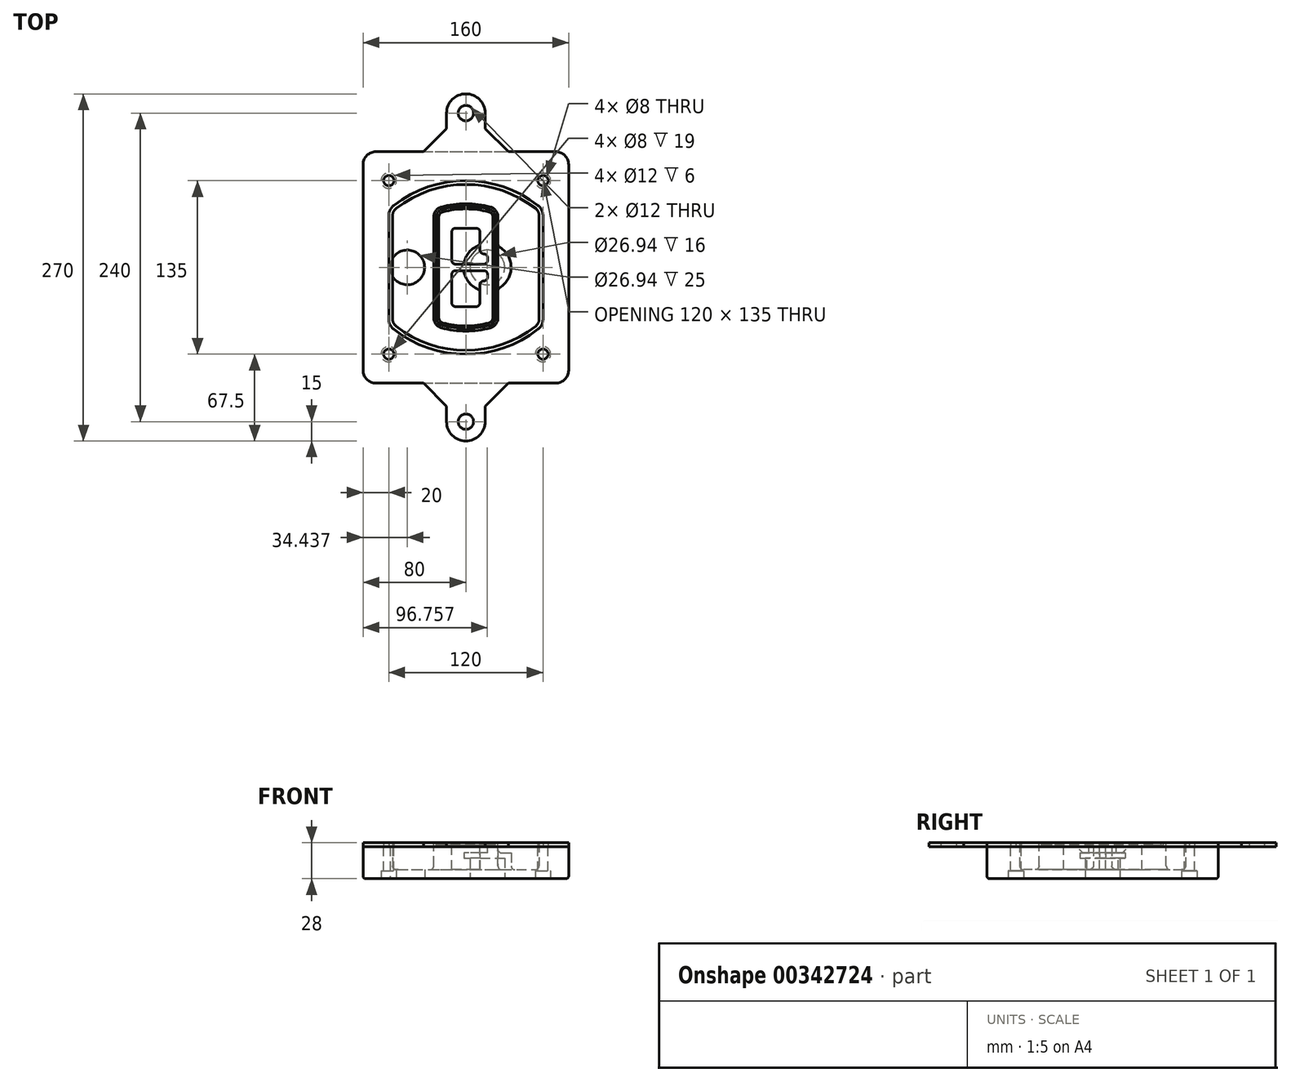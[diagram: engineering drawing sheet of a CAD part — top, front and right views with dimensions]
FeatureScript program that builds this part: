
annotation { "Feature Type Name" : "Feature", "Feature Type Description" : "" }
export const myFeature = defineFeature(function(context is Context, id is Id, definition is map)
    precondition{}
    {
        {
            var Q0;
            Q0=qCreatedBy(makeId("Top.planeOp"),FACE);
            var sketch = newSketch(context, id + "F0", { "sketchPlane" : qUnion([Q0])});
            skPoint(sketch, "E0.rect.middle", {"position": v(0, 0) * mm});
            skLineSegment(sketch, "E1.bottom", {"start": v(-70, -90) * mm, "end": v(70, -90) * mm});
            skLineSegment(sketch, "E1.top", {"start": v(-70, 90) * mm, "end": v(70, 90) * mm});
            skLineSegment(sketch, "E1.left", {"start": v(-80, -80) * mm, "end": v(-80, 80) * mm});
            skLineSegment(sketch, "E1.right", {"start": v(80, -80) * mm, "end": v(80, 80) * mm});
            skLineSegment(sketch, "E2", {"start": v(-80, 90) * mm, "end": v(80, -90) * mm, "construction": true});
            skLineSegment(sketch, "E3", {"start": v(80, 90) * mm, "end": v(-80, -90) * mm, "construction": true});
            skCircle(sketch, "E4", {"center": v(-60, 67.5) * mm, "radius": 4 * mm});
            skCircle(sketch, "E5", {"center": v(60, 67.5) * mm, "radius": 4 * mm});
            skCircle(sketch, "E6", {"center": v(60, -67.5) * mm, "radius": 4 * mm});
            skCircle(sketch, "E7", {"center": v(-60, -67.5) * mm, "radius": 4 * mm});
            skLineSegment(sketch, "E8", {"start": v(-60, 67.5) * mm, "end": v(60, 67.5) * mm, "construction": true});
            skLineSegment(sketch, "E9", {"start": v(60, 67.5) * mm, "end": v(60, -67.5) * mm, "construction": true});
            skLineSegment(sketch, "E10", {"start": v(60, -67.5) * mm, "end": v(-60, -67.5) * mm, "construction": true});
            skLineSegment(sketch, "E11", {"start": v(-60, -67.5) * mm, "end": v(-60, 67.5) * mm, "construction": true});
            skLineSegment(sketch, "E12", {"start": v(-60, 40.3) * mm, "end": v(-60, -40.3) * mm});
            skLineSegment(sketch, "E13", {"start": v(60, 40.3) * mm, "end": v(60, -40.3) * mm});
            skArc(sketch, "E14", {"start": v(56.15, 48.18) * mm, "mid": v(0, 67.5) * mm, "end": v(-56.15, 48.18) * mm});
            skArc(sketch, "E15", {"start": v(-56.15, -48.18) * mm, "mid": v(0, -67.5) * mm, "end": v(56.15, -48.18) * mm});
            skLineSegment(sketch, "E16", {"start": v(-60, 0) * mm, "end": v(60, 0) * mm, "construction": true});
            skPoint(sketch, "E17.visualSharp", {"position": v(-60, -45) * mm});
            skArc(sketch, "E17.filletArc", {"start": v(-60, -40.3) * mm, "mid": v(-58.99, -44.68) * mm, "end": v(-56.15, -48.18) * mm});
            skPoint(sketch, "E18.visualSharp", {"position": v(-60, 45) * mm});
            skArc(sketch, "E18.filletArc", {"start": v(-56.15, 48.18) * mm, "mid": v(-58.99, 44.68) * mm, "end": v(-60, 40.3) * mm});
            skPoint(sketch, "E19.visualSharp", {"position": v(60, 45) * mm});
            skArc(sketch, "E19.filletArc", {"start": v(60, 40.3) * mm, "mid": v(58.99, 44.68) * mm, "end": v(56.15, 48.18) * mm});
            skPoint(sketch, "E20.visualSharp", {"position": v(60, -45) * mm});
            skArc(sketch, "E20.filletArc", {"start": v(56.15, -48.18) * mm, "mid": v(58.99, -44.68) * mm, "end": v(60, -40.3) * mm});
            skPoint(sketch, "E21.visualSharp", {"position": v(-80, 90) * mm});
            skArc(sketch, "E21.filletArc", {"start": v(-70, 90) * mm, "mid": v(-77.07, 87.07) * mm, "end": v(-80, 80) * mm});
            skPoint(sketch, "E22.visualSharp", {"position": v(80, 90) * mm});
            skArc(sketch, "E22.filletArc", {"start": v(80, 80) * mm, "mid": v(77.07, 87.07) * mm, "end": v(70, 90) * mm});
            skPoint(sketch, "E23.visualSharp", {"position": v(80, -90) * mm});
            skArc(sketch, "E23.filletArc", {"start": v(70, -90) * mm, "mid": v(77.07, -87.07) * mm, "end": v(80, -80) * mm});
            skPoint(sketch, "E24.visualSharp", {"position": v(-80, -90) * mm});
            skArc(sketch, "E24.filletArc", {"start": v(-80, -80) * mm, "mid": v(-77.07, -87.07) * mm, "end": v(-70, -90) * mm});
            skArc(sketch, "E25.0", {"start": v(57, 40.3) * mm, "mid": v(56.3, 43.36) * mm, "end": v(54.3, 45.81) * mm});
            skLineSegment(sketch, "E25.1", {"start": v(57, 40.3) * mm, "end": v(57, -40.3) * mm});
            skArc(sketch, "E25.2", {"start": v(54.3, -45.81) * mm, "mid": v(56.3, -43.36) * mm, "end": v(57, -40.3) * mm});
            skArc(sketch, "E25.3", {"start": v(-54.3, -45.81) * mm, "mid": v(0, -64.5) * mm, "end": v(54.3, -45.81) * mm});
            skArc(sketch, "E25.4", {"start": v(-57, -40.3) * mm, "mid": v(-56.3, -43.36) * mm, "end": v(-54.3, -45.81) * mm});
            skArc(sketch, "E25.5", {"start": v(54.3, 45.81) * mm, "mid": v(0, 64.5) * mm, "end": v(-54.3, 45.81) * mm});
            skLineSegment(sketch, "E25.6", {"start": v(-57, 40.3) * mm, "end": v(-57, -40.3) * mm});
            skArc(sketch, "E25.7", {"start": v(-54.3, 45.81) * mm, "mid": v(-56.3, 43.36) * mm, "end": v(-57, 40.3) * mm});
            skArc(sketch, "E26.0", {"start": v(-58.62, 51.33) * mm, "mid": v(-62.58, 46.43) * mm, "end": v(-64, 40.3) * mm});
            skArc(sketch, "E26.1", {"start": v(58.62, 51.33) * mm, "mid": v(0, 71.5) * mm, "end": v(-58.62, 51.33) * mm});
            skArc(sketch, "E26.2", {"start": v(64, 40.3) * mm, "mid": v(62.58, 46.43) * mm, "end": v(58.62, 51.33) * mm});
            skLineSegment(sketch, "E26.3", {"start": v(64, 40.3) * mm, "end": v(64, -40.3) * mm});
            skArc(sketch, "E26.4", {"start": v(58.62, -51.33) * mm, "mid": v(62.58, -46.43) * mm, "end": v(64, -40.3) * mm});
            skLineSegment(sketch, "E26.5", {"start": v(-64, 40.3) * mm, "end": v(-64, -40.3) * mm});
            skArc(sketch, "E26.6", {"start": v(-58.62, -51.33) * mm, "mid": v(0, -71.5) * mm, "end": v(58.62, -51.33) * mm});
            skArc(sketch, "E26.7", {"start": v(-64, -40.3) * mm, "mid": v(-62.58, -46.43) * mm, "end": v(-58.62, -51.33) * mm});
            skSolve(sketch);
        }
        {
            var Q0;
            Q0=makeQuery(id+"F0.imprint","IMPRINT",FACE,{"disambiguationData":[TD([[makeQuery(id+"F0.imprint","IMPRINT",EDGE,{"derivedFrom":sQuery(id+"F0.wireOp",EDGE,"E1.bottom")}),1.0]])]});
            var Q1;
            Q1=makeQuery(id+"F0.imprint","IMPRINT",FACE,{"disambiguationData":[TD([[makeQuery(id+"F0.imprint","IMPRINT",EDGE,{"derivedFrom":sQuery(id+"F0.wireOp",EDGE,"E12")}),1.0]])]});
            var Q2;
            Q2=makeQuery(id+"F0.imprint","IMPRINT",FACE,{"disambiguationData":[TD([[makeQuery(id+"F0.imprint","IMPRINT",EDGE,{"derivedFrom":sQuery(id+"F0.wireOp",EDGE,"E25.0")}),1.0]])]});
            var Q3;
            Q3=makeQuery(id+"F0.imprint","IMPRINT",FACE,{"disambiguationData":[TD([[makeQuery(id+"F0.imprint","IMPRINT",EDGE,{"derivedFrom":sQuery(id+"F0.wireOp",EDGE,"E12")}),-1.0]])]});
            extrude(context, id + "F1", {"entities" : qUnion([Q0, Q1, Q2, Q3]), "oppositeDirection" : true, "depth" : 25 * mm});
        }
        {
            var Q0;
            Q0=makeQuery(id+"F0.imprint","IMPRINT",FACE,{"disambiguationData":[TD([[makeQuery(id+"F0.imprint","IMPRINT",EDGE,{"derivedFrom":sQuery(id+"F0.wireOp",EDGE,"E12")}),1.0]])]});
            extrude(context, id + "F2", {"entities" : qUnion([Q0]), "operationType" : NewBodyOperationType.ADD, "depth" : 3 * mm});
        }
        {
            var Q0;
            Q0=makeQuery(id+"F0.imprint","IMPRINT",FACE,{"disambiguationData":[TD([[makeQuery(id+"F0.imprint","IMPRINT",EDGE,{"derivedFrom":sQuery(id+"F0.wireOp",EDGE,"E25.0")}),1.0]])]});
            extrude(context, id + "F3", {"entities" : qUnion([Q0]), "operationType" : NewBodyOperationType.REMOVE, "oppositeDirection" : true, "depth" : 18 * mm});
        }
        {
            var Q0;
            Q0=makeQuery(id+"F2.opExtrude","CAP_FACE",FACE,{"disambiguationData":[OSD([sQuery(id+"F0.wireOp",EDGE,"E12"),sQuery(id+"F0.wireOp",EDGE,"E13"),sQuery(id+"F0.wireOp",EDGE,"E14"),sQuery(id+"F0.wireOp",EDGE,"E15"),sQuery(id+"F0.wireOp",EDGE,"E17.filletArc"),sQuery(id+"F0.wireOp",EDGE,"E18.filletArc"),sQuery(id+"F0.wireOp",EDGE,"E19.filletArc"),sQuery(id+"F0.wireOp",EDGE,"E20.filletArc"),sQuery(id+"F0.wireOp",EDGE,"E25.0"),sQuery(id+"F0.wireOp",EDGE,"E25.1"),sQuery(id+"F0.wireOp",EDGE,"E25.2"),sQuery(id+"F0.wireOp",EDGE,"E25.3"),sQuery(id+"F0.wireOp",EDGE,"E25.4"),sQuery(id+"F0.wireOp",EDGE,"E25.5"),sQuery(id+"F0.wireOp",EDGE,"E25.6"),sQuery(id+"F0.wireOp",EDGE,"E25.7")])],"isStart":false});
            var sketch = newSketch(context, id + "F4", { "sketchPlane" : qUnion([Q0])});
            skArc(sketch, "E27.0", {"start": v(-19.08, -46.97) * mm, "mid": v(0, -49.5) * mm, "end": v(19.08, -46.97) * mm});
            skArc(sketch, "E28.0", {"start": v(19.08, 46.97) * mm, "mid": v(0, 49.5) * mm, "end": v(-19.08, 46.97) * mm});
            skLineSegment(sketch, "E29", {"start": v(-25, 39.25) * mm, "end": v(-25, -39.25) * mm});
            skLineSegment(sketch, "E30", {"start": v(25, 39.25) * mm, "end": v(25, -39.25) * mm});
            skLineSegment(sketch, "E31", {"start": v(-25, 45.1) * mm, "end": v(25, 45.1) * mm, "construction": true});
            skLineSegment(sketch, "E32", {"start": v(-25, -45.1) * mm, "end": v(25, -45.1) * mm, "construction": true});
            skPoint(sketch, "E33.visualSharp", {"position": v(-25, 45.1) * mm});
            skArc(sketch, "E33.filletArc", {"start": v(-19.08, 46.97) * mm, "mid": v(-23.35, 44.11) * mm, "end": v(-25, 39.25) * mm});
            skPoint(sketch, "E34.visualSharp", {"position": v(25, 45.1) * mm});
            skArc(sketch, "E34.filletArc", {"start": v(25, 39.25) * mm, "mid": v(23.35, 44.11) * mm, "end": v(19.08, 46.97) * mm});
            skPoint(sketch, "E35.visualSharp", {"position": v(25, -45.1) * mm});
            skArc(sketch, "E35.filletArc", {"start": v(19.08, -46.97) * mm, "mid": v(23.35, -44.11) * mm, "end": v(25, -39.25) * mm});
            skPoint(sketch, "E36.visualSharp", {"position": v(-25, -45.1) * mm});
            skArc(sketch, "E36.filletArc", {"start": v(-25, -39.25) * mm, "mid": v(-23.35, -44.11) * mm, "end": v(-19.08, -46.97) * mm});
            skArc(sketch, "E37.0", {"start": v(54.3, 45.81) * mm, "mid": v(0, 64.5) * mm, "end": v(-54.3, 45.81) * mm});
            skArc(sketch, "E37.1", {"start": v(-54.3, 45.81) * mm, "mid": v(-56.3, 43.36) * mm, "end": v(-57, 40.3) * mm});
            skLineSegment(sketch, "E37.2", {"start": v(-57, 40.3) * mm, "end": v(-57, -40.3) * mm});
            skArc(sketch, "E37.3", {"start": v(-57, -40.3) * mm, "mid": v(-56.3, -43.36) * mm, "end": v(-54.3, -45.81) * mm});
            skArc(sketch, "E37.4", {"start": v(-54.3, -45.81) * mm, "mid": v(0, -64.5) * mm, "end": v(54.3, -45.81) * mm});
            skArc(sketch, "E37.5", {"start": v(54.3, -45.81) * mm, "mid": v(56.3, -43.36) * mm, "end": v(57, -40.3) * mm});
            skLineSegment(sketch, "E37.6", {"start": v(57, 40.3) * mm, "end": v(57, -40.3) * mm});
            skArc(sketch, "E37.7", {"start": v(57, 40.3) * mm, "mid": v(56.3, 43.36) * mm, "end": v(54.3, 45.81) * mm});
            skLineSegment(sketch, "E38.0", {"start": v(23, 39.25) * mm, "end": v(23, -39.25) * mm});
            skArc(sketch, "E38.1", {"start": v(18.56, -45.04) * mm, "mid": v(21.76, -42.9) * mm, "end": v(23, -39.25) * mm});
            skArc(sketch, "E38.2", {"start": v(-18.56, -45.04) * mm, "mid": v(0, -47.5) * mm, "end": v(18.56, -45.04) * mm});
            skArc(sketch, "E38.3", {"start": v(-23, -39.25) * mm, "mid": v(-21.76, -42.9) * mm, "end": v(-18.56, -45.04) * mm});
            skLineSegment(sketch, "E38.4", {"start": v(-23, 39.25) * mm, "end": v(-23, -39.25) * mm});
            skArc(sketch, "E38.5", {"start": v(23, 39.25) * mm, "mid": v(21.76, 42.9) * mm, "end": v(18.56, 45.04) * mm});
            skArc(sketch, "E38.6", {"start": v(-18.56, 45.04) * mm, "mid": v(-21.76, 42.9) * mm, "end": v(-23, 39.25) * mm});
            skArc(sketch, "E38.7", {"start": v(18.56, 45.04) * mm, "mid": v(0, 47.5) * mm, "end": v(-18.56, 45.04) * mm});
            skArc(sketch, "E39.0", {"start": v(21, 39.25) * mm, "mid": v(20.18, 41.68) * mm, "end": v(18.04, 43.1) * mm});
            skLineSegment(sketch, "E39.1", {"start": v(21, 39.25) * mm, "end": v(21, -39.25) * mm});
            skArc(sketch, "E39.2", {"start": v(18.04, -43.1) * mm, "mid": v(20.18, -41.68) * mm, "end": v(21, -39.25) * mm});
            skArc(sketch, "E39.3", {"start": v(-18.04, -43.1) * mm, "mid": v(0, -45.5) * mm, "end": v(18.04, -43.1) * mm});
            skArc(sketch, "E39.4", {"start": v(-21, -39.25) * mm, "mid": v(-20.18, -41.68) * mm, "end": v(-18.04, -43.1) * mm});
            skArc(sketch, "E39.5", {"start": v(18.04, 43.1) * mm, "mid": v(0, 45.5) * mm, "end": v(-18.04, 43.1) * mm});
            skLineSegment(sketch, "E39.6", {"start": v(-21, 39.25) * mm, "end": v(-21, -39.25) * mm});
            skArc(sketch, "E39.7", {"start": v(-18.04, 43.1) * mm, "mid": v(-20.18, 41.68) * mm, "end": v(-21, 39.25) * mm});
            skLineSegment(sketch, "E40", {"start": v(-25, 0) * mm, "end": v(25, 0) * mm, "construction": true});
            skLineSegment(sketch, "E41", {"start": v(-11, 5.5) * mm, "end": v(-11, 27.5) * mm});
            skLineSegment(sketch, "E42", {"start": v(-8, 30.5) * mm, "end": v(8, 30.5) * mm});
            skLineSegment(sketch, "E43", {"start": v(11, 27.5) * mm, "end": v(11, 13.5) * mm});
            skLineSegment(sketch, "E44", {"start": v(14, 10.5) * mm, "end": v(14, 10.5) * mm});
            skLineSegment(sketch, "E45", {"start": v(17, 7.5) * mm, "end": v(17, 5.5) * mm});
            skLineSegment(sketch, "E46", {"start": v(14, 2.5) * mm, "end": v(-8, 2.5) * mm});
            skPoint(sketch, "E47.visualSharp", {"position": v(-11, 30.5) * mm});
            skArc(sketch, "E47.filletArc", {"start": v(-8, 30.5) * mm, "mid": v(-10.12, 29.62) * mm, "end": v(-11, 27.5) * mm});
            skPoint(sketch, "E48.visualSharp", {"position": v(11, 30.5) * mm});
            skArc(sketch, "E48.filletArc", {"start": v(11, 27.5) * mm, "mid": v(10.12, 29.62) * mm, "end": v(8, 30.5) * mm});
            skPoint(sketch, "E49.visualSharp", {"position": v(11, 10.5) * mm});
            skArc(sketch, "E49.filletArc", {"start": v(11, 13.5) * mm, "mid": v(11.88, 11.38) * mm, "end": v(14, 10.5) * mm});
            skPoint(sketch, "E50.visualSharp", {"position": v(17, 10.5) * mm});
            skArc(sketch, "E50.filletArc", {"start": v(17, 7.5) * mm, "mid": v(16.12, 9.62) * mm, "end": v(14, 10.5) * mm});
            skPoint(sketch, "E51.visualSharp", {"position": v(17, 2.5) * mm});
            skArc(sketch, "E51.filletArc", {"start": v(14, 2.5) * mm, "mid": v(16.12, 3.38) * mm, "end": v(17, 5.5) * mm});
            skPoint(sketch, "E52.visualSharp", {"position": v(-11, 2.5) * mm});
            skArc(sketch, "E52.filletArc", {"start": v(-11, 5.5) * mm, "mid": v(-10.12, 3.38) * mm, "end": v(-8, 2.5) * mm});
            skLineSegment(sketch, "E53.0.MirrorCS", {"start": v(14, -2.5) * mm, "end": v(-8, -2.5) * mm});
            skArc(sketch, "E54.0.MirrorCS", {"start": v(-11, -5.5) * mm, "mid": v(-10.12, -3.38) * mm, "end": v(-8, -2.5) * mm});
            skLineSegment(sketch, "E55.0.MirrorCS", {"start": v(-11, -5.5) * mm, "end": v(-11, -27.5) * mm});
            skArc(sketch, "E56.0.MirrorCS", {"start": v(-8, -30.5) * mm, "mid": v(-10.12, -29.62) * mm, "end": v(-11, -27.5) * mm});
            skLineSegment(sketch, "E57.0.MirrorCS", {"start": v(-8, -30.5) * mm, "end": v(8, -30.5) * mm});
            skArc(sketch, "E58.0.MirrorCS", {"start": v(11, -27.5) * mm, "mid": v(10.12, -29.62) * mm, "end": v(8, -30.5) * mm});
            skLineSegment(sketch, "E59.0.MirrorCS", {"start": v(11, -27.5) * mm, "end": v(11, -13.5) * mm});
            skArc(sketch, "E60.0.MirrorCS", {"start": v(11, -13.5) * mm, "mid": v(11.88, -11.38) * mm, "end": v(14, -10.5) * mm});
            skArc(sketch, "E61.0.MirrorCS", {"start": v(17, -7.5) * mm, "mid": v(16.12, -9.62) * mm, "end": v(14, -10.5) * mm});
            skLineSegment(sketch, "E62.0.MirrorCS", {"start": v(17, -7.5) * mm, "end": v(17, -5.5) * mm});
            skArc(sketch, "E63.0.MirrorCS", {"start": v(14, -2.5) * mm, "mid": v(16.12, -3.38) * mm, "end": v(17, -5.5) * mm});
            skSolve(sketch);
        }
        {
            var Q0;
            Q0=makeQuery(id+"F4.imprint","IMPRINT",FACE,{"disambiguationData":[TD([[makeQuery(id+"F4.imprint","IMPRINT",EDGE,{"derivedFrom":sQuery(id+"F4.wireOp",EDGE,"E27.0")}),1.0]])]});
            var Q1;
            Q1=makeQuery(id+"F4.imprint","IMPRINT",FACE,{"disambiguationData":[TD([[makeQuery(id+"F4.imprint","IMPRINT",EDGE,{"derivedFrom":sQuery(id+"F4.wireOp",EDGE,"E38.0")}),-1.0]])]});
            var Q2;
            Q2=makeQuery(id+"F4.imprint","IMPRINT",FACE,{"disambiguationData":[TD([[makeQuery(id+"F4.imprint","IMPRINT",EDGE,{"derivedFrom":sQuery(id+"F4.wireOp",EDGE,"E39.0")}),1.0]])]});
            extrude(context, id + "F5", {"entities" : qUnion([Q0, Q1, Q2]), "operationType" : NewBodyOperationType.ADD, "endBound" : BoundingType.UP_TO_NEXT, "oppositeDirection" : true, "depth" : 25 * mm});
        }
        {
            var Q0;
            Q0=makeQuery(id+"F4.imprint","IMPRINT",FACE,{"disambiguationData":[TD([[makeQuery(id+"F4.imprint","IMPRINT",EDGE,{"derivedFrom":sQuery(id+"F4.wireOp",EDGE,"E38.0")}),-1.0]])]});
            extrude(context, id + "F6", {"entities" : qUnion([Q0]), "operationType" : NewBodyOperationType.REMOVE, "oppositeDirection" : true, "depth" : 2 * mm});
        }
        {
            var Q0;
            Q0=makeQuery(id+"F1.opExtrude","CAP_FACE",FACE,{"disambiguationData":[OSD([sQuery(id+"F0.wireOp",EDGE,"E1.bottom"),sQuery(id+"F0.wireOp",EDGE,"E1.top"),sQuery(id+"F0.wireOp",EDGE,"E1.left"),sQuery(id+"F0.wireOp",EDGE,"E1.right"),sQuery(id+"F0.wireOp",EDGE,"E4"),sQuery(id+"F0.wireOp",EDGE,"E5"),sQuery(id+"F0.wireOp",EDGE,"E6"),sQuery(id+"F0.wireOp",EDGE,"E7"),sQuery(id+"F0.wireOp",EDGE,"E21.filletArc"),sQuery(id+"F0.wireOp",EDGE,"E22.filletArc"),sQuery(id+"F0.wireOp",EDGE,"E23.filletArc"),sQuery(id+"F0.wireOp",EDGE,"E24.filletArc")])],"isStart":false});
            var sketch = newSketch(context, id + "F7", { "sketchPlane" : qUnion([Q0])});
            skCircle(sketch, "E64", {"center": v(16.76, 0) * mm, "radius": 13.47 * mm});
            skCircle(sketch, "E65", {"center": v(-45.56, 0) * mm, "radius": 13.47 * mm});
            skLineSegment(sketch, "E66", {"start": v(80, 0) * mm, "end": v(-80, 0) * mm});
            skCircle(sketch, "E67", {"center": v(16.76, 0) * mm, "radius": 18.47 * mm});
            skCircle(sketch, "E68", {"center": v(60, -67.5) * mm, "radius": 6 * mm});
            skCircle(sketch, "E69", {"center": v(-60, -67.5) * mm, "radius": 6 * mm});
            skCircle(sketch, "E70", {"center": v(-60, 67.5) * mm, "radius": 6 * mm});
            skCircle(sketch, "E71", {"center": v(60, 67.5) * mm, "radius": 6 * mm});
            skSolve(sketch);
        }
        {
            var Q0;
            {var subQ1=sQuery(id+"F7.wireOp",EDGE,"E66");var subQ4=sQuery(id+"F7.wireOp",EDGE,"E64");var subQ6=makeQuery(id+"F7.imprint","INTERSECT",VERTEX,{"disambiguationData":[OD(0.0)],"derivedFrom":[subQ4,subQ1]});Q0=makeQuery(id+"F7.imprint","IMPRINT",FACE,{"disambiguationData":[TD([[makeQuery(id+"F7.imprint","IMPRINT",EDGE,{"disambiguationData":[TD([[subQ6,-1.0]])],"derivedFrom":subQ4}),-1.0]])]});}
            var Q1;
            {var subQ0=sQuery(id+"F7.wireOp",EDGE,"E66");var subQ1=sQuery(id+"F7.wireOp",EDGE,"E64");var subQ3=makeQuery(id+"F7.imprint","INTERSECT",VERTEX,{"disambiguationData":[OD(0.0)],"derivedFrom":[subQ1,subQ0]});Q1=makeQuery(id+"F7.imprint","IMPRINT",FACE,{"disambiguationData":[TD([[makeQuery(id+"F7.imprint","IMPRINT",EDGE,{"disambiguationData":[TD([[subQ3,-1.0]])],"derivedFrom":subQ1}),1.0]])]});}
            var Q2;
            {var subQ0=sQuery(id+"F7.wireOp",EDGE,"E66");var subQ1=sQuery(id+"F7.wireOp",EDGE,"E64");var subQ3=makeQuery(id+"F7.imprint","INTERSECT",VERTEX,{"disambiguationData":[OD(0.0)],"derivedFrom":[subQ1,subQ0]});Q2=makeQuery(id+"F7.imprint","IMPRINT",FACE,{"disambiguationData":[TD([[makeQuery(id+"F7.imprint","IMPRINT",EDGE,{"disambiguationData":[TD([[subQ3,1.0]])],"derivedFrom":subQ1}),1.0]])]});}
            var Q3;
            {var subQ1=sQuery(id+"F7.wireOp",EDGE,"E66");var subQ4=sQuery(id+"F7.wireOp",EDGE,"E64");var subQ6=makeQuery(id+"F7.imprint","INTERSECT",VERTEX,{"disambiguationData":[OD(0.0)],"derivedFrom":[subQ4,subQ1]});Q3=makeQuery(id+"F7.imprint","IMPRINT",FACE,{"disambiguationData":[TD([[makeQuery(id+"F7.imprint","IMPRINT",EDGE,{"disambiguationData":[TD([[subQ6,1.0]])],"derivedFrom":subQ4}),-1.0]])]});}
            extrude(context, id + "F8", {"entities" : qUnion([Q0, Q1, Q2, Q3]), "operationType" : NewBodyOperationType.ADD, "oppositeDirection" : true, "depth" : 20 * mm});
        }
        {
            var Q0;
            {var subQ0=sQuery(id+"F7.wireOp",EDGE,"E66");var subQ1=sQuery(id+"F7.wireOp",EDGE,"E64");var subQ3=makeQuery(id+"F7.imprint","INTERSECT",VERTEX,{"disambiguationData":[OD(0.0)],"derivedFrom":[subQ1,subQ0]});Q0=makeQuery(id+"F7.imprint","IMPRINT",FACE,{"disambiguationData":[TD([[makeQuery(id+"F7.imprint","IMPRINT",EDGE,{"disambiguationData":[TD([[subQ3,-1.0]])],"derivedFrom":subQ1}),1.0]])]});}
            var Q1;
            {var subQ0=sQuery(id+"F7.wireOp",EDGE,"E66");var subQ1=sQuery(id+"F7.wireOp",EDGE,"E64");var subQ3=makeQuery(id+"F7.imprint","INTERSECT",VERTEX,{"disambiguationData":[OD(0.0)],"derivedFrom":[subQ1,subQ0]});Q1=makeQuery(id+"F7.imprint","IMPRINT",FACE,{"disambiguationData":[TD([[makeQuery(id+"F7.imprint","IMPRINT",EDGE,{"disambiguationData":[TD([[subQ3,1.0]])],"derivedFrom":subQ1}),1.0]])]});}
            extrude(context, id + "F9", {"entities" : qUnion([Q0, Q1]), "operationType" : NewBodyOperationType.REMOVE, "oppositeDirection" : true, "depth" : 16 * mm});
        }
        {
            var Q0;
            {var subQ0=sQuery(id+"F7.wireOp",EDGE,"E66");var subQ1=sQuery(id+"F7.wireOp",EDGE,"E65");var subQ3=makeQuery(id+"F7.imprint","INTERSECT",VERTEX,{"disambiguationData":[OD(0.0)],"derivedFrom":[subQ1,subQ0]});Q0=makeQuery(id+"F7.imprint","IMPRINT",FACE,{"disambiguationData":[TD([[makeQuery(id+"F7.imprint","IMPRINT",EDGE,{"disambiguationData":[TD([[subQ3,-1.0]])],"derivedFrom":subQ1}),1.0]])]});}
            var Q1;
            {var subQ0=sQuery(id+"F7.wireOp",EDGE,"E66");var subQ1=sQuery(id+"F7.wireOp",EDGE,"E65");var subQ3=makeQuery(id+"F7.imprint","INTERSECT",VERTEX,{"disambiguationData":[OD(0.0)],"derivedFrom":[subQ1,subQ0]});Q1=makeQuery(id+"F7.imprint","IMPRINT",FACE,{"disambiguationData":[TD([[makeQuery(id+"F7.imprint","IMPRINT",EDGE,{"disambiguationData":[TD([[subQ3,1.0]])],"derivedFrom":subQ1}),1.0]])]});}
            extrude(context, id + "F10", {"entities" : qUnion([Q0, Q1]), "operationType" : NewBodyOperationType.REMOVE, "oppositeDirection" : true, "depth" : 25 * mm});
        }
        {
            var Q0;
            Q0=makeQuery(id+"F7.imprint","IMPRINT",FACE,{"disambiguationData":[TD([[makeQuery(id+"F7.imprint","IMPRINT",EDGE,{"derivedFrom":sQuery(id+"F7.wireOp",EDGE,"E68")}),1.0]])]});
            var Q1;
            Q1=makeQuery(id+"F7.imprint","IMPRINT",FACE,{"disambiguationData":[TD([[makeQuery(id+"F7.imprint","IMPRINT",EDGE,{"derivedFrom":makeQuery(id+"F1.opExtrude","CAP_EDGE",EDGE,{"disambiguationData":[OSD([sQuery(id+"F0.wireOp",EDGE,"E5")])],"isStart":false})}),-1.0]])]});
            var Q2;
            Q2=makeQuery(id+"F7.imprint","IMPRINT",FACE,{"disambiguationData":[TD([[makeQuery(id+"F7.imprint","IMPRINT",EDGE,{"derivedFrom":sQuery(id+"F7.wireOp",EDGE,"E69")}),1.0]])]});
            var Q3;
            Q3=makeQuery(id+"F7.imprint","IMPRINT",FACE,{"disambiguationData":[TD([[makeQuery(id+"F7.imprint","IMPRINT",EDGE,{"derivedFrom":makeQuery(id+"F1.opExtrude","CAP_EDGE",EDGE,{"disambiguationData":[OSD([sQuery(id+"F0.wireOp",EDGE,"E4")])],"isStart":false})}),-1.0]])]});
            var Q4;
            Q4=makeQuery(id+"F7.imprint","IMPRINT",FACE,{"disambiguationData":[TD([[makeQuery(id+"F7.imprint","IMPRINT",EDGE,{"derivedFrom":sQuery(id+"F7.wireOp",EDGE,"E70")}),1.0]])]});
            var Q5;
            Q5=makeQuery(id+"F7.imprint","IMPRINT",FACE,{"disambiguationData":[TD([[makeQuery(id+"F7.imprint","IMPRINT",EDGE,{"derivedFrom":makeQuery(id+"F1.opExtrude","CAP_EDGE",EDGE,{"disambiguationData":[OSD([sQuery(id+"F0.wireOp",EDGE,"E7")])],"isStart":false})}),-1.0]])]});
            var Q6;
            Q6=makeQuery(id+"F7.imprint","IMPRINT",FACE,{"disambiguationData":[TD([[makeQuery(id+"F7.imprint","IMPRINT",EDGE,{"derivedFrom":sQuery(id+"F7.wireOp",EDGE,"E71")}),1.0]])]});
            var Q7;
            Q7=makeQuery(id+"F7.imprint","IMPRINT",FACE,{"disambiguationData":[TD([[makeQuery(id+"F7.imprint","IMPRINT",EDGE,{"derivedFrom":makeQuery(id+"F1.opExtrude","CAP_EDGE",EDGE,{"disambiguationData":[OSD([sQuery(id+"F0.wireOp",EDGE,"E6")])],"isStart":false})}),-1.0]])]});
            extrude(context, id + "F11", {"entities" : qUnion([Q0, Q1, Q2, Q3, Q4, Q5, Q6, Q7]), "operationType" : NewBodyOperationType.REMOVE, "oppositeDirection" : true, "depth" : 6 * mm});
        }
        {
            var Q0;
            Q0=makeQuery(id+"F9.boolean.opBoolean","COPY",FACE,{"derivedFrom":makeQuery(id+"F9.opExtrude","CAP_FACE",FACE,{"disambiguationData":[OSD([sQuery(id+"F7.wireOp",EDGE,"E64")])],"isStart":false})});
            var sketch = newSketch(context, id + "F12", { "sketchPlane" : qUnion([Q0])});
            skArc(sketch, "E72.0", {"start": v(11, 17.55) * mm, "mid": v(2.57, 11.82) * mm, "end": v(-1.54, 2.5) * mm});
            skArc(sketch, "E72.1", {"start": v(-1.54, -2.5) * mm, "mid": v(2.57, -11.82) * mm, "end": v(11, -17.55) * mm});
            skLineSegment(sketch, "E73", {"start": v(-1.54, -2.5) * mm, "end": v(14, -2.5) * mm});
            skLineSegment(sketch, "E74.0", {"start": v(14, 2.5) * mm, "end": v(-1.54, 2.5) * mm});
            skArc(sketch, "E74.1", {"start": v(14, 2.5) * mm, "mid": v(16.12, 3.38) * mm, "end": v(17, 5.5) * mm});
            skLineSegment(sketch, "E74.2", {"start": v(17, 7.5) * mm, "end": v(17, 5.5) * mm});
            skArc(sketch, "E74.3", {"start": v(17, 7.5) * mm, "mid": v(16.12, 9.62) * mm, "end": v(14, 10.5) * mm});
            skArc(sketch, "E74.4", {"start": v(11, 13.5) * mm, "mid": v(11.88, 11.38) * mm, "end": v(14, 10.5) * mm});
            skLineSegment(sketch, "E74.5", {"start": v(11, 17.55) * mm, "end": v(11, 13.5) * mm});
            skLineSegment(sketch, "E74.7", {"start": v(14, -2.5) * mm, "end": v(-1.54, -2.5) * mm});
            skArc(sketch, "E74.8", {"start": v(14, -2.5) * mm, "mid": v(16.12, -3.38) * mm, "end": v(17, -5.5) * mm});
            skLineSegment(sketch, "E74.9", {"start": v(17, -7.5) * mm, "end": v(17, -5.5) * mm});
            skArc(sketch, "E74.10", {"start": v(17, -7.5) * mm, "mid": v(16.12, -9.62) * mm, "end": v(14, -10.5) * mm});
            skArc(sketch, "E74.11", {"start": v(11, -13.5) * mm, "mid": v(11.88, -11.38) * mm, "end": v(14, -10.5) * mm});
            skLineSegment(sketch, "E74.12", {"start": v(11, -17.55) * mm, "end": v(11, -13.5) * mm});
            skPoint(sketch, "E75.orphan", {"position": v(11, -27.5) * mm});
            skPoint(sketch, "E76.orphan", {"position": v(-8, -2.5) * mm});
            skPoint(sketch, "E77.orphan", {"position": v(-8, 2.5) * mm});
            skPoint(sketch, "E78.orphan", {"position": v(11, 27.5) * mm});
            skSolve(sketch);
        }
        {
            var Q0;
            {var subQ7=sQuery(id+"F12.wireOp",EDGE,"E72.0");var subQ14=sQuery(id+"F12.wireOp",EDGE,"E72.1");var subQ16=sQuery(id+"F12.wireOp",EDGE,"E74.1");var subQ18=sQuery(id+"F12.wireOp",EDGE,"E74.8");Q0=qUnion([makeQuery(id+"F12.imprint","IMPRINT",FACE,{"disambiguationData":[TD([[makeQuery(id+"F12.imprint","IMPRINT",EDGE,{"derivedFrom":subQ7}),1.0]])]}),makeQuery(id+"F12.imprint","IMPRINT",FACE,{"disambiguationData":[TD([[makeQuery(id+"F12.imprint","IMPRINT",EDGE,{"derivedFrom":subQ14}),1.0]])]}),makeQuery(id+"F12.imprint","IMPRINT",FACE,{"disambiguationData":[TD([[makeQuery(id+"F12.imprint","IMPRINT",EDGE,{"derivedFrom":subQ16}),1.0]])]}),makeQuery(id+"F12.imprint","IMPRINT",FACE,{"disambiguationData":[TD([[makeQuery(id+"F12.imprint","IMPRINT",EDGE,{"derivedFrom":subQ18}),-1.0]])]})]);}
            var Q1;
            Q1=makeQuery(id+"F5.boolean.opBoolean","SPLIT",FACE,{"disambiguationData":[TD([makeQuery(id+"F5.opExtrude","SWEPT_FACE",FACE,{"disambiguationData":[OSD([sQuery(id+"F4.wireOp",EDGE,"E41")])]})])],"derivedFrom":makeQuery(id+"F3.boolean.opBoolean","COPY",FACE,{"derivedFrom":makeQuery(id+"F3.opExtrude","CAP_FACE",FACE,{"disambiguationData":[OSD([sQuery(id+"F0.wireOp",EDGE,"E25.0"),sQuery(id+"F0.wireOp",EDGE,"E25.1"),sQuery(id+"F0.wireOp",EDGE,"E25.2"),sQuery(id+"F0.wireOp",EDGE,"E25.3"),sQuery(id+"F0.wireOp",EDGE,"E25.4"),sQuery(id+"F0.wireOp",EDGE,"E25.5"),sQuery(id+"F0.wireOp",EDGE,"E25.6"),sQuery(id+"F0.wireOp",EDGE,"E25.7")])],"isStart":false})})});
            extrude(context, id + "F13", {"entities" : qUnion([Q0]), "operationType" : NewBodyOperationType.REMOVE, "endBound" : BoundingType.UP_TO_SURFACE, "endBoundEntityFace" : qUnion([Q1]), "depth" : 25 * mm});
        }
        {
            var Q0;
            Q0=makeQuery(id+"F3.boolean.opBoolean","COPY",EDGE,{"derivedFrom":makeQuery(id+"F3.opExtrude","CAP_EDGE",EDGE,{"disambiguationData":[OSD([sQuery(id+"F0.wireOp",EDGE,"E25.6")])],"isStart":false})});
            var Q1;
            Q1=makeQuery(id+"F8.boolean.opBoolean","INTERSECT",EDGE,{"derivedFrom":[makeQuery(id+"F5.opExtrude","SWEPT_FACE",FACE,{"disambiguationData":[OSD([sQuery(id+"F4.wireOp",EDGE,"E30")])]}),makeQuery(id+"F8.opExtrude","CAP_FACE",FACE,{"disambiguationData":[OSD([sQuery(id+"F7.wireOp",EDGE,"E67")])],"isStart":false})]});
            var Q2;
            Q2=makeQuery(id+"F8.boolean.opBoolean","INTERSECT",EDGE,{"disambiguationData":[OD(1.0)],"derivedFrom":[makeQuery(id+"F5.opExtrude","SWEPT_FACE",FACE,{"disambiguationData":[OSD([sQuery(id+"F4.wireOp",EDGE,"E30")])]}),makeQuery(id+"F8.opExtrude","SWEPT_FACE",FACE,{"disambiguationData":[OSD([sQuery(id+"F7.wireOp",EDGE,"E67")])]})]});
            var Q3;
            {var subQ0=sQuery(id+"F4.wireOp",EDGE,"E30");Q3=makeQuery(id+"F8.boolean.opBoolean","SPLIT",EDGE,{"disambiguationData":[TD([makeQuery(id+"F5.opExtrude","SWEPT_FACE",FACE,{"disambiguationData":[OSD([sQuery(id+"F4.wireOp",EDGE,"E35.filletArc")])]})])],"derivedFrom":makeQuery(id+"F5.opExtrude","CAP_EDGE",EDGE,{"disambiguationData":[OSD([subQ0])],"isStart":false})});}
            var Q4;
            {var subQ0=sQuery(id+"F0.wireOp",EDGE,"E25.7");var subQ1=sQuery(id+"F0.wireOp",EDGE,"E25.1");var subQ2=sQuery(id+"F0.wireOp",EDGE,"E25.6");var subQ3=sQuery(id+"F0.wireOp",EDGE,"E25.5");var subQ4=sQuery(id+"F0.wireOp",EDGE,"E25.4");var subQ5=sQuery(id+"F0.wireOp",EDGE,"E25.0");var subQ6=sQuery(id+"F0.wireOp",EDGE,"E25.2");var subQ7=sQuery(id+"F0.wireOp",EDGE,"E25.3");Q4=makeQuery(id+"F8.boolean.opBoolean","INTERSECT",EDGE,{"derivedFrom":[makeQuery(id+"F5.boolean.opBoolean","SPLIT",FACE,{"disambiguationData":[TD([makeQuery(id+"F2.opExtrude","SWEPT_FACE",FACE,{"disambiguationData":[OSD([subQ5])]})])],"derivedFrom":makeQuery(id+"F3.boolean.opBoolean","COPY",FACE,{"derivedFrom":makeQuery(id+"F3.opExtrude","CAP_FACE",FACE,{"disambiguationData":[OSD([subQ5,subQ1,subQ6,subQ7,subQ4,subQ3,subQ2,subQ0])],"isStart":false})})}),makeQuery(id+"F8.opExtrude","SWEPT_FACE",FACE,{"disambiguationData":[OSD([sQuery(id+"F7.wireOp",EDGE,"E67")])]})]});}
            var Q5;
            Q5=makeQuery(id+"F8.boolean.opBoolean","INTERSECT",EDGE,{"disambiguationData":[OD(0.0)],"derivedFrom":[makeQuery(id+"F5.opExtrude","SWEPT_FACE",FACE,{"disambiguationData":[OSD([sQuery(id+"F4.wireOp",EDGE,"E30")])]}),makeQuery(id+"F8.opExtrude","SWEPT_FACE",FACE,{"disambiguationData":[OSD([sQuery(id+"F7.wireOp",EDGE,"E67")])]})]});
            fillet(context, id + "F14", {"entities" : qUnion([Q0, Q1, Q2, Q3, Q4, Q5]), "radius" : 3 * mm, "tangentPropagation" : true, "allowEdgeOverflow" : false});
        }
        {
            var Q0;
            Q0=makeQuery(id+"F1.opExtrude","CAP_EDGE",EDGE,{"disambiguationData":[OSD([sQuery(id+"F0.wireOp",EDGE,"E1.bottom")])],"isStart":false});
            fillet(context, id + "F15", {"entities" : qUnion([Q0]), "radius" : 2 * mm, "tangentPropagation" : true, "allowEdgeOverflow" : false});
        }
        {
            var Q0;
            {var subQ0=sQuery(id+"F0.wireOp",EDGE,"E21.filletArc");var subQ1=sQuery(id+"F0.wireOp",EDGE,"E7");var subQ2=sQuery(id+"F0.wireOp",EDGE,"E6");var subQ3=sQuery(id+"F0.wireOp",EDGE,"E5");var subQ4=sQuery(id+"F0.wireOp",EDGE,"E4");var subQ5=sQuery(id+"F0.wireOp",EDGE,"E22.filletArc");var subQ6=sQuery(id+"F0.wireOp",EDGE,"E1.bottom");var subQ7=sQuery(id+"F0.wireOp",EDGE,"E1.right");var subQ8=sQuery(id+"F0.wireOp",EDGE,"E1.top");var subQ9=sQuery(id+"F0.wireOp",EDGE,"E1.left");var subQ10=sQuery(id+"F0.wireOp",EDGE,"E23.filletArc");var subQ11=sQuery(id+"F0.wireOp",EDGE,"E24.filletArc");Q0=makeQuery(id+"F2.boolean.opBoolean","SPLIT",FACE,{"disambiguationData":[TD([makeQuery(id+"F1.opExtrude","SWEPT_FACE",FACE,{"disambiguationData":[OSD([subQ6])]})])],"derivedFrom":makeQuery(id+"F1.opExtrude","CAP_FACE",FACE,{"disambiguationData":[OSD([subQ6,subQ8,subQ9,subQ7,subQ4,subQ3,subQ2,subQ1,subQ0,subQ5,subQ10,subQ11])],"isStart":true})});}
            var sketch = newSketch(context, id + "F16", { "sketchPlane" : qUnion([Q0])});
            skLineSegment(sketch, "E79.0", {"start": v(80, -80) * mm, "end": v(80, 80) * mm});
            skArc(sketch, "E79.1", {"start": v(80, 80) * mm, "mid": v(77.07, 87.07) * mm, "end": v(70, 90) * mm});
            skArc(sketch, "E79.2", {"start": v(-70, 90) * mm, "mid": v(-77.07, 87.07) * mm, "end": v(-80, 80) * mm});
            skLineSegment(sketch, "E79.3", {"start": v(-70, 90) * mm, "end": v(70, 90) * mm});
            skCircle(sketch, "E79.4", {"center": v(-60, 67.5) * mm, "radius": 4 * mm});
            skCircle(sketch, "E79.5", {"center": v(-60, -67.5) * mm, "radius": 4 * mm});
            skLineSegment(sketch, "E79.6", {"start": v(-80, -80) * mm, "end": v(-80, 80) * mm});
            skArc(sketch, "E79.7", {"start": v(-80, -80) * mm, "mid": v(-77.07, -87.07) * mm, "end": v(-70, -90) * mm});
            skLineSegment(sketch, "E79.8", {"start": v(-70, -90) * mm, "end": v(70, -90) * mm});
            skLineSegment(sketch, "E79.9", {"start": v(-60, 40.3) * mm, "end": v(-60, -40.3) * mm});
            skArc(sketch, "E79.10", {"start": v(-56.15, 48.18) * mm, "mid": v(-58.99, 44.68) * mm, "end": v(-60, 40.3) * mm});
            skArc(sketch, "E79.11", {"start": v(56.15, 48.18) * mm, "mid": v(0, 67.5) * mm, "end": v(-56.15, 48.18) * mm});
            skArc(sketch, "E79.12", {"start": v(60, 40.3) * mm, "mid": v(58.99, 44.68) * mm, "end": v(56.15, 48.18) * mm});
            skLineSegment(sketch, "E79.13", {"start": v(60, 40.3) * mm, "end": v(60, -40.3) * mm});
            skArc(sketch, "E79.14", {"start": v(56.15, -48.18) * mm, "mid": v(58.99, -44.68) * mm, "end": v(60, -40.3) * mm});
            skArc(sketch, "E79.15", {"start": v(-56.15, -48.18) * mm, "mid": v(0, -67.5) * mm, "end": v(56.15, -48.18) * mm});
            skArc(sketch, "E79.16", {"start": v(-60, -40.3) * mm, "mid": v(-58.99, -44.68) * mm, "end": v(-56.15, -48.18) * mm});
            skCircle(sketch, "E79.17", {"center": v(60, -67.5) * mm, "radius": 4 * mm});
            skCircle(sketch, "E79.18", {"center": v(60, 67.5) * mm, "radius": 4 * mm});
            skArc(sketch, "E79.19", {"start": v(70, -90) * mm, "mid": v(77.07, -87.07) * mm, "end": v(80, -80) * mm});
            skLineSegment(sketch, "E80", {"start": v(0, 90) * mm, "end": v(0, 120) * mm, "construction": true});
            skCircle(sketch, "E81", {"center": v(0, 120) * mm, "radius": 6 * mm});
            skLineSegment(sketch, "E82", {"start": v(-33, 90) * mm, "end": v(-15, 108) * mm});
            skLineSegment(sketch, "E83", {"start": v(33, 90) * mm, "end": v(15, 108) * mm});
            skLineSegment(sketch, "E84", {"start": v(15, 108) * mm, "end": v(15, 120) * mm});
            skLineSegment(sketch, "E85", {"start": v(-15, 108) * mm, "end": v(-15, 120) * mm});
            skArc(sketch, "E86", {"start": v(-15, 120) * mm, "mid": v(0, 135) * mm, "end": v(15, 120) * mm});
            skLineSegment(sketch, "E87", {"start": v(-80, 0) * mm, "end": v(80, 0) * mm, "construction": true});
            skLineSegment(sketch, "E88.MirrorCS", {"start": v(-33, -90) * mm, "end": v(-15, -108) * mm});
            skLineSegment(sketch, "E89.MirrorCS", {"start": v(15, -108) * mm, "end": v(15, -120) * mm});
            skLineSegment(sketch, "E90.MirrorCS", {"start": v(33, -90) * mm, "end": v(15, -108) * mm});
            skArc(sketch, "E91.MirrorCS", {"start": v(-15, -120) * mm, "mid": v(0, -135) * mm, "end": v(15, -120) * mm});
            skCircle(sketch, "E92.MirrorC", {"center": v(0, -120) * mm, "radius": 6 * mm});
            skLineSegment(sketch, "E93.MirrorCS", {"start": v(0, -90) * mm, "end": v(0, -120) * mm, "construction": true});
            skLineSegment(sketch, "E94.MirrorCS", {"start": v(-15, -108) * mm, "end": v(-15, -120) * mm});
            skSolve(sketch);
        }
        {
            var Q0;
            Q0=makeQuery(id+"F16.imprint","IMPRINT",FACE,{"disambiguationData":[TD([[makeQuery(id+"F16.imprint","IMPRINT",EDGE,{"derivedFrom":sQuery(id+"F16.wireOp",EDGE,"E81")}),-1.0]])]});
            var Q1;
            {var subQ1=sQuery(id+"F16.wireOp",EDGE,"E88.MirrorCS");Q1=makeQuery(id+"F16.imprint","IMPRINT",FACE,{"disambiguationData":[TD([[makeQuery(id+"F16.imprint","IMPRINT",EDGE,{"derivedFrom":subQ1}),1.0]])]});}
            var Q2;
            Q2=makeQuery(id+"F16.imprint","IMPRINT",FACE,{"disambiguationData":[TD([[makeQuery(id+"F16.imprint","IMPRINT",EDGE,{"derivedFrom":sQuery(id+"F16.wireOp",EDGE,"E79.0")}),1.0]])]});
            var Q3;
            Q3=makeQuery(id+"F2.opExtrude","CAP_FACE",FACE,{"disambiguationData":[OSD([sQuery(id+"F0.wireOp",EDGE,"E12"),sQuery(id+"F0.wireOp",EDGE,"E13"),sQuery(id+"F0.wireOp",EDGE,"E14"),sQuery(id+"F0.wireOp",EDGE,"E15"),sQuery(id+"F0.wireOp",EDGE,"E17.filletArc"),sQuery(id+"F0.wireOp",EDGE,"E18.filletArc"),sQuery(id+"F0.wireOp",EDGE,"E19.filletArc"),sQuery(id+"F0.wireOp",EDGE,"E20.filletArc"),sQuery(id+"F0.wireOp",EDGE,"E25.0"),sQuery(id+"F0.wireOp",EDGE,"E25.1"),sQuery(id+"F0.wireOp",EDGE,"E25.2"),sQuery(id+"F0.wireOp",EDGE,"E25.3"),sQuery(id+"F0.wireOp",EDGE,"E25.4"),sQuery(id+"F0.wireOp",EDGE,"E25.5"),sQuery(id+"F0.wireOp",EDGE,"E25.6"),sQuery(id+"F0.wireOp",EDGE,"E25.7")])],"isStart":false});
            extrude(context, id + "F17", {"entities" : qUnion([Q0, Q1, Q2]), "endBound" : BoundingType.UP_TO_SURFACE, "endBoundEntityFace" : qUnion([Q3]), "depth" : 25 * mm});
        }
    });
